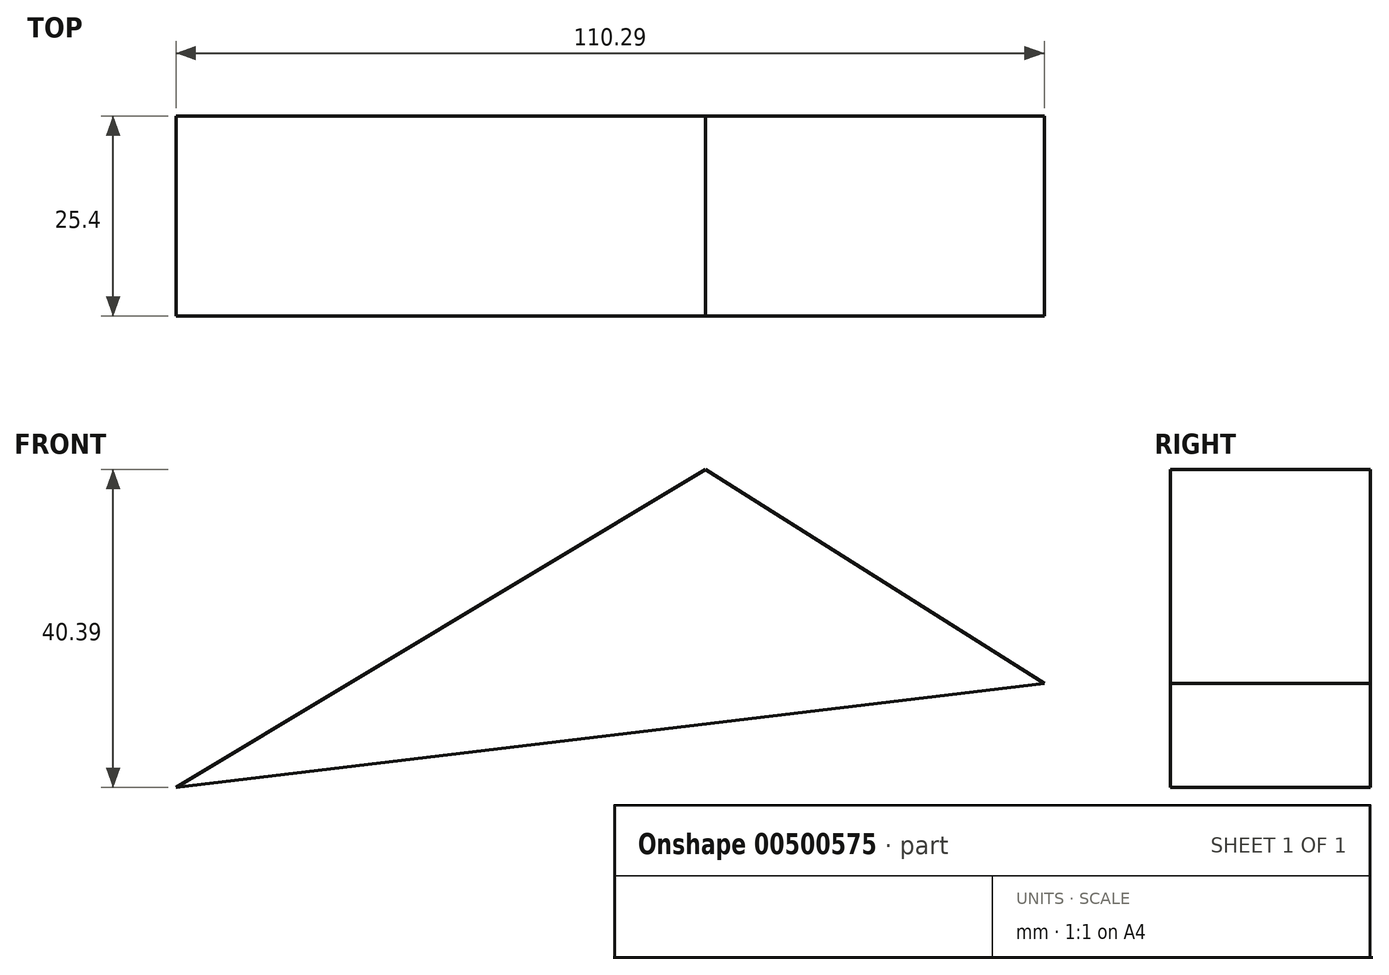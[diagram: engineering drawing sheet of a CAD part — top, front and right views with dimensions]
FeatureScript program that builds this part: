
annotation { "Feature Type Name" : "Feature", "Feature Type Description" : "" }
export const myFeature = defineFeature(function(context is Context, id is Id, definition is map)
    precondition{}
    {
        {
            var Q0;
            Q0=qCreatedBy(makeId("Front.planeOp"),FACE);
            var sketch = newSketch(context, id + "F0", { "sketchPlane" : qUnion([Q0])});
            skLineSegment(sketch, "E0", {"start": v(-105.45, -13.22) * mm, "end": v(-38.2, 27.17) * mm});
            skLineSegment(sketch, "E1", {"start": v(-38.2, 27.17) * mm, "end": v(4.84, 0) * mm});
            skLineSegment(sketch, "E2", {"start": v(4.84, 0) * mm, "end": v(-105.45, -13.22) * mm});
            skSolve(sketch);
        }
        {
            var Q0;
            Q0=makeQuery(id+"F0.imprint","IMPRINT",FACE,{"disambiguationData":[TD([[makeQuery(id+"F0.imprint","IMPRINT",EDGE,{"derivedFrom":sQuery(id+"F0.wireOp",EDGE,"E0")}),-1.0]])]});
            extrude(context, id + "F1", {"entities" : qUnion([Q0]), "depth" : 25.4 * mm});
        }
    });
